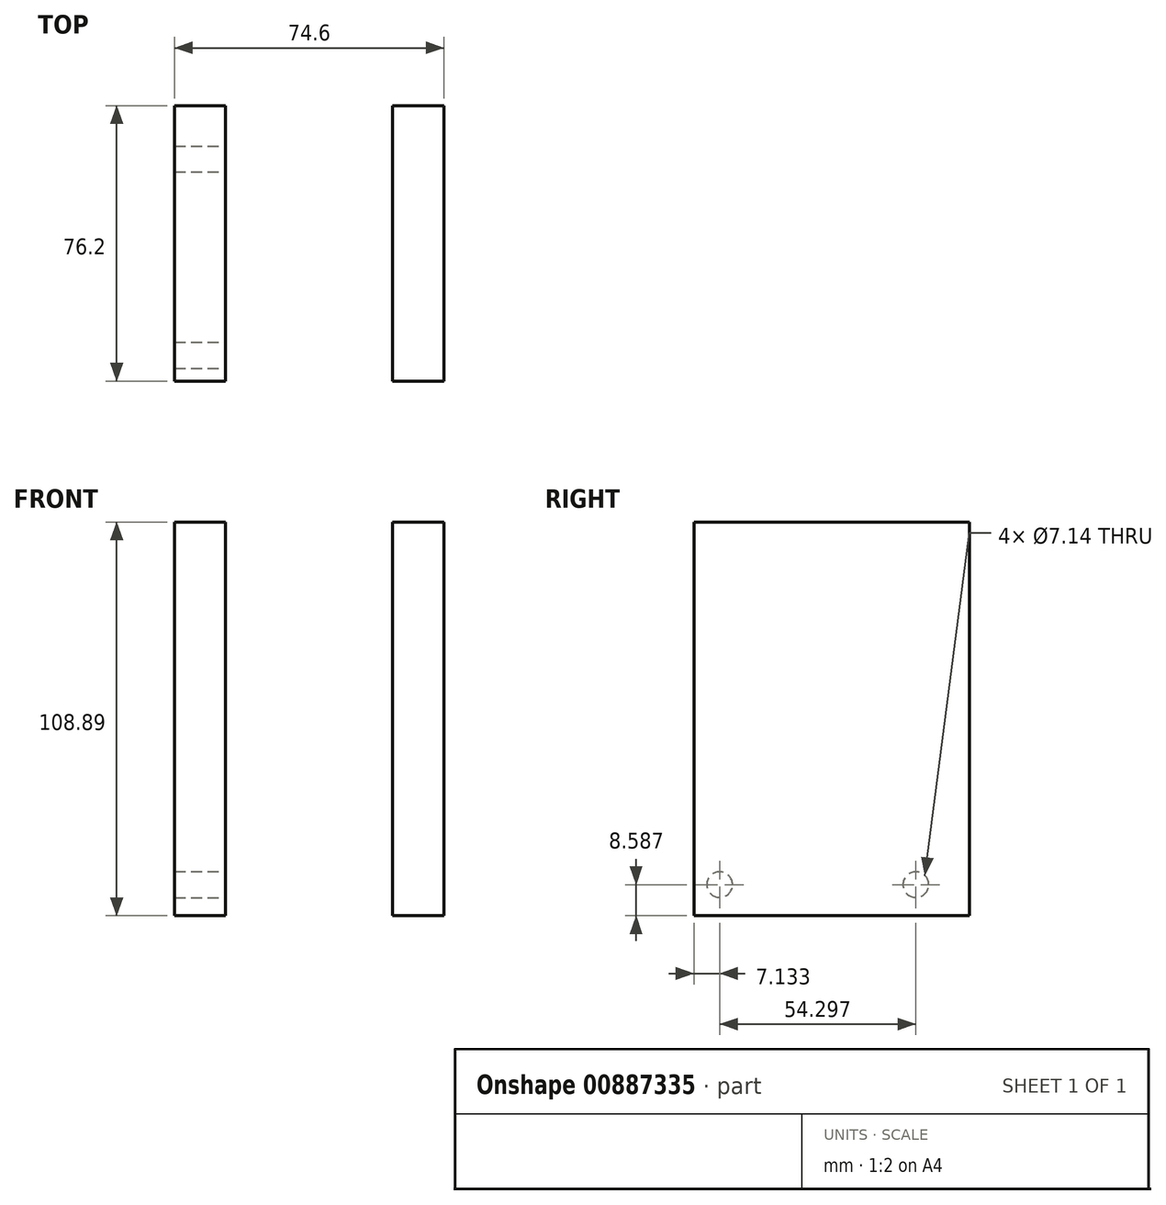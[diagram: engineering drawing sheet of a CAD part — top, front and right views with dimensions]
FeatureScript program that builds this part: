
annotation { "Feature Type Name" : "Feature", "Feature Type Description" : "" }
export const myFeature = defineFeature(function(context is Context, id is Id, definition is map)
    precondition{}
    {
        {
            var Q0;
            Q0=qCreatedBy(makeId("Front.planeOp"),FACE);
            var sketch = newSketch(context, id + "F0", { "sketchPlane" : qUnion([Q0])});
            skLineSegment(sketch, "E0.bottom", {"start": v(-60.3, 52.79) * mm, "end": v(-46.17, 52.79) * mm});
            skLineSegment(sketch, "E0.top", {"start": v(-60.3, -56.1) * mm, "end": v(-46.17, -56.1) * mm});
            skLineSegment(sketch, "E0.left", {"start": v(-60.3, 52.79) * mm, "end": v(-60.3, -56.1) * mm});
            skLineSegment(sketch, "E0.right", {"start": v(-46.17, 52.79) * mm, "end": v(-46.17, -56.1) * mm});
            skLineSegment(sketch, "E1.bottom", {"start": v(14.29, 52.79) * mm, "end": v(0, 52.79) * mm});
            skLineSegment(sketch, "E1.top", {"start": v(14.29, -56.1) * mm, "end": v(0, -56.1) * mm});
            skLineSegment(sketch, "E1.left", {"start": v(14.29, 52.79) * mm, "end": v(14.29, -56.1) * mm});
            skLineSegment(sketch, "E1.right", {"start": v(0, 52.79) * mm, "end": v(0, -56.1) * mm});
            skSolve(sketch);
        }
        {
            var Q0;
            Q0=makeQuery(id+"F0.imprint","IMPRINT",FACE,{"disambiguationData":[TD([[makeQuery(id+"F0.imprint","IMPRINT",EDGE,{"derivedFrom":sQuery(id+"F0.wireOp",EDGE,"E0.bottom")}),-1.0]])]});
            var Q1;
            Q1=makeQuery(id+"F0.imprint","IMPRINT",FACE,{"disambiguationData":[TD([[makeQuery(id+"F0.imprint","IMPRINT",EDGE,{"derivedFrom":sQuery(id+"F0.wireOp",EDGE,"E1.bottom")}),1.0]])]});
            extrude(context, id + "F1", {"entities" : qUnion([Q0, Q1]), "depth" : 76.2 * mm, "offsetDistance" : 25.4 * mm});
        }
        {
            var Q0;
            Q0=makeQuery(id+"F1.opExtrude","SWEPT_FACE",FACE,{"disambiguationData":[OSD([sQuery(id+"F0.wireOp",EDGE,"E0.right")])]});
            var sketch = newSketch(context, id + "F2", { "sketchPlane" : qUnion([Q0])});
            skCircle(sketch, "E2", {"center": v(-69.07, -47.51) * mm, "radius": 1.94 * mm});
            skCircle(sketch, "E3", {"center": v(-14.77, -47.51) * mm, "radius": 1.94 * mm});
            skSolve(sketch);
        }
        {
            var Q0;
            Q0=sQuery(id+"F2.wireOp",VERTEX,"E2.center");
            var Q1;
            Q1=sQuery(id+"F2.wireOp",VERTEX,"E3.center");
            var Q2;
            Q2=makeQuery(id+"F1.opExtrude","SWEPT_BODY",BODY,{"disambiguationData":[OSD([sQuery(id+"F0.wireOp",EDGE,"E0.bottom"),sQuery(id+"F0.wireOp",EDGE,"E0.top"),sQuery(id+"F0.wireOp",EDGE,"E0.left"),sQuery(id+"F0.wireOp",EDGE,"E0.right")])]});
            hole(context, id + "F3", {"style" : HoleStyle.SIMPLE, "endStyle" : HoleEndStyle.THROUGH, "holeDiameter" : 7.14 * mm, "majorDiameter" : 6.35 * mm, "isTappedThrough" : true, "tappedDepth" : 12.7 * mm, "tapClearance" : 3, "locations" : qUnion([Q0, Q1]), "scope" : qUnion([Q2])});
        }
    });
